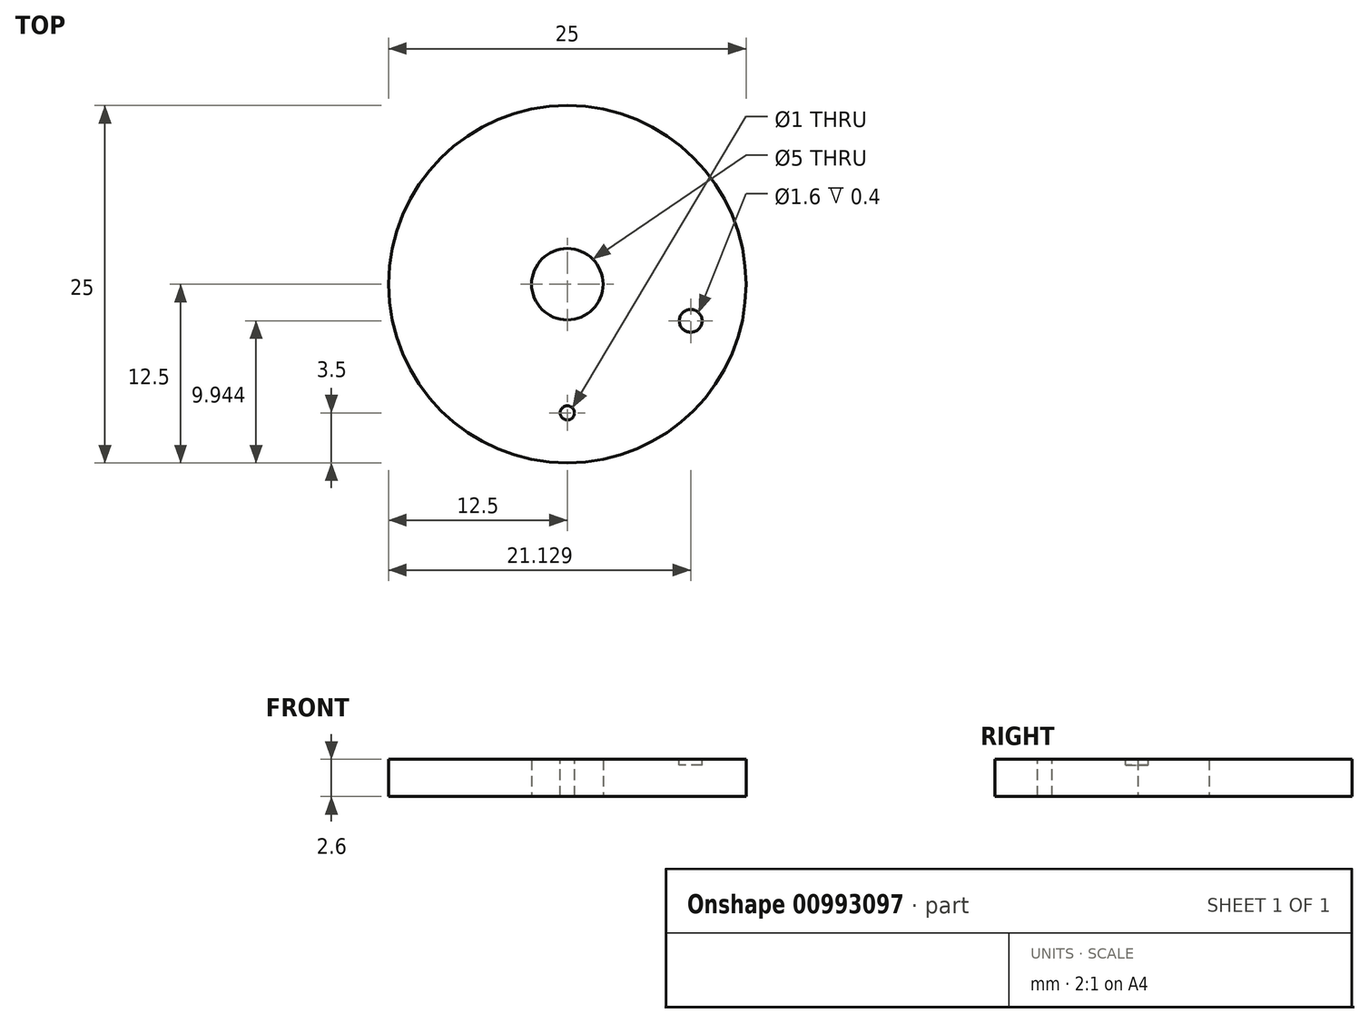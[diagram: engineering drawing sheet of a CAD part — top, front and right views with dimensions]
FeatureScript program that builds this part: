
annotation { "Feature Type Name" : "Feature", "Feature Type Description" : "" }
export const myFeature = defineFeature(function(context is Context, id is Id, definition is map)
    precondition{}
    {
        {
            var Q0;
            Q0=qCreatedBy(makeId("Top.planeOp"),FACE);
            var sketch = newSketch(context, id + "F0", { "sketchPlane" : qUnion([Q0])});
            skCircle(sketch, "E0", {"center": v(0, 0) * mm, "radius": 12.5 * mm});
            skSolve(sketch);
        }
        {
            var Q0;
            Q0 = qSketchRegion(id + "F0", true);
            extrude(context, id + "F1", {"entities" : qUnion([Q0]), "depth" : 2.6 * mm, "offsetDistance" : 25 * mm});
        }
        {
            var Q0;
            Q0=qCreatedBy(makeId("Right.planeOp"),FACE);
            var sketch = newSketch(context, id + "F2", { "sketchPlane" : qUnion([Q0])});
            skLineSegment(sketch, "E1", {"start": v(0, 0) * mm, "end": v(0, 57.27) * mm});
            skSolve(sketch);
        }
        {
            var Q0;
            Q0=makeQuery(id+"F1.opExtrude","CAP_FACE",FACE,{"disambiguationData":[OSD([sQuery(id+"F0.wireOp",EDGE,"E0")])],"isStart":false});
            var sketch = newSketch(context, id + "F3", { "sketchPlane" : qUnion([Q0])});
            skLineSegment(sketch, "E2", {"start": v(0, 0) * mm, "end": v(0, -9) * mm});
            skSolve(sketch);
        }
        {
            var Q0;
            Q0=makeQuery(id+"F3.imprint","IMPRINT",FACE,{"disambiguationData":[TD([[makeQuery(id+"F3.imprint","IMPRINT",EDGE,{"derivedFrom":makeQuery(id+"F1.opExtrude","CAP_EDGE",EDGE,{"disambiguationData":[OSD([sQuery(id+"F0.wireOp",EDGE,"E0")])],"isStart":false})}),1.0]])]});
            var sketch = newSketch(context, id + "F4", { "sketchPlane" : qUnion([Q0])});
            skCircle(sketch, "E3", {"center": v(0, -9) * mm, "radius": 0.5 * mm});
            skSolve(sketch);
        }
        {
            var Q0;
            Q0 = qSketchRegion(id + "F4", true);
            extrude(context, id + "F5", {"entities" : qUnion([Q0]), "operationType" : NewBodyOperationType.REMOVE, "oppositeDirection" : true, "depth" : 25 * mm, "offsetDistance" : 25 * mm});
        }
        {
            var Q0;
            Q0=makeQuery(id+"F1.opExtrude","CAP_FACE",FACE,{"disambiguationData":[OSD([sQuery(id+"F0.wireOp",EDGE,"E0")])],"isStart":true});
            var sketch = newSketch(context, id + "F6", { "sketchPlane" : qUnion([Q0])});
            skCircle(sketch, "E4", {"center": v(0, 0) * mm, "radius": 2.5 * mm});
            skSolve(sketch);
        }
        {
            var Q0;
            Q0 = qSketchRegion(id + "F6", true);
            extrude(context, id + "F7", {"entities" : qUnion([Q0]), "operationType" : NewBodyOperationType.REMOVE, "oppositeDirection" : true, "depth" : 25 * mm, "offsetDistance" : 25 * mm});
        }
        {
            var Q0;
            Q0=makeQuery(id+"F3.imprint","IMPRINT",FACE,{"disambiguationData":[TD([[makeQuery(id+"F3.imprint","IMPRINT",EDGE,{"derivedFrom":makeQuery(id+"F1.opExtrude","CAP_EDGE",EDGE,{"disambiguationData":[OSD([sQuery(id+"F0.wireOp",EDGE,"E0")])],"isStart":false})}),1.0]])]});
            var sketch = newSketch(context, id + "F8", { "sketchPlane" : qUnion([Q0])});
            skCircle(sketch, "E5", {"center": v(8.63, -2.56) * mm, "radius": 0.8 * mm});
            skSolve(sketch);
        }
        {
            var Q0;
            Q0 = qSketchRegion(id + "F8", true);
            extrude(context, id + "F9", {"entities" : qUnion([Q0]), "operationType" : NewBodyOperationType.REMOVE, "oppositeDirection" : true, "depth" : .4 * mm, "offsetDistance" : 25 * mm});
        }
    });
